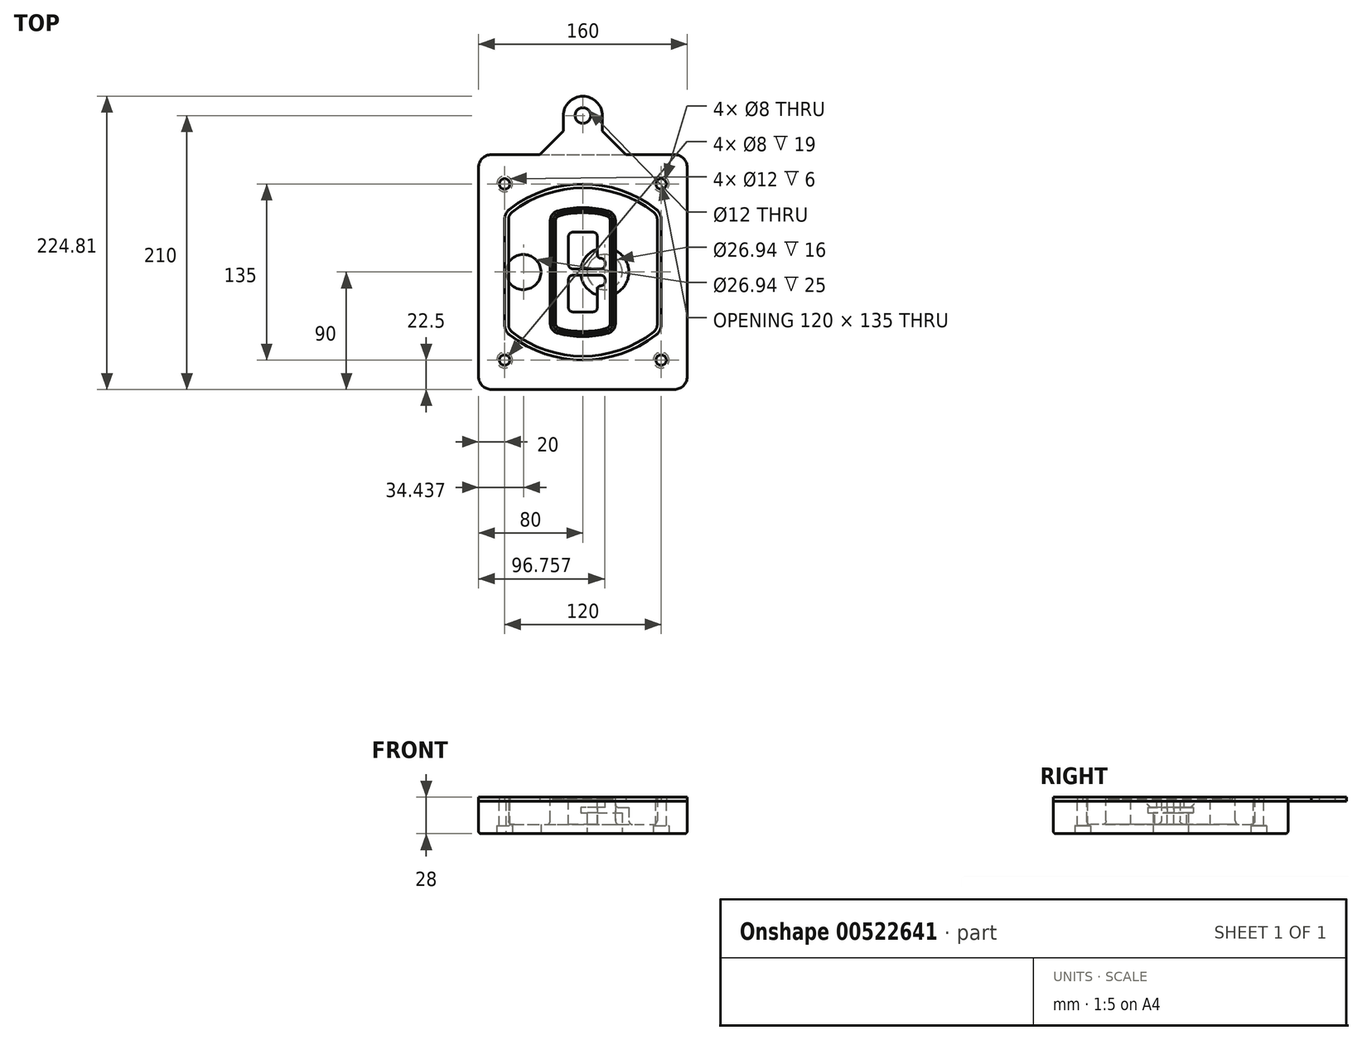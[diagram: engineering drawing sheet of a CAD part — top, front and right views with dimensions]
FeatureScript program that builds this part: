
annotation { "Feature Type Name" : "Feature", "Feature Type Description" : "" }
export const myFeature = defineFeature(function(context is Context, id is Id, definition is map)
    precondition{}
    {
        {
            var Q0;
            Q0=qCreatedBy(makeId("Top.planeOp"),FACE);
            var sketch = newSketch(context, id + "F0", { "sketchPlane" : qUnion([Q0])});
            skPoint(sketch, "E0.rect.middle", {"position": v(0, 0) * mm});
            skLineSegment(sketch, "E1.bottom", {"start": v(-70, -90) * mm, "end": v(70, -90) * mm});
            skLineSegment(sketch, "E1.top", {"start": v(-70, 90) * mm, "end": v(70, 90) * mm});
            skLineSegment(sketch, "E1.left", {"start": v(-80, -80) * mm, "end": v(-80, 80) * mm});
            skLineSegment(sketch, "E1.right", {"start": v(80, -80) * mm, "end": v(80, 80) * mm});
            skLineSegment(sketch, "E2", {"start": v(-80, 90) * mm, "end": v(80, -90) * mm, "construction": true});
            skLineSegment(sketch, "E3", {"start": v(80, 90) * mm, "end": v(-80, -90) * mm, "construction": true});
            skCircle(sketch, "E4", {"center": v(-60, 67.5) * mm, "radius": 4 * mm});
            skCircle(sketch, "E5", {"center": v(60, 67.5) * mm, "radius": 4 * mm});
            skCircle(sketch, "E6", {"center": v(60, -67.5) * mm, "radius": 4 * mm});
            skCircle(sketch, "E7", {"center": v(-60, -67.5) * mm, "radius": 4 * mm});
            skLineSegment(sketch, "E8", {"start": v(-60, 67.5) * mm, "end": v(60, 67.5) * mm, "construction": true});
            skLineSegment(sketch, "E9", {"start": v(60, 67.5) * mm, "end": v(60, -67.5) * mm, "construction": true});
            skLineSegment(sketch, "E10", {"start": v(60, -67.5) * mm, "end": v(-60, -67.5) * mm, "construction": true});
            skLineSegment(sketch, "E11", {"start": v(-60, -67.5) * mm, "end": v(-60, 67.5) * mm, "construction": true});
            skLineSegment(sketch, "E12", {"start": v(-60, 40.3) * mm, "end": v(-60, -40.3) * mm});
            skLineSegment(sketch, "E13", {"start": v(60, 40.3) * mm, "end": v(60, -40.3) * mm});
            skArc(sketch, "E14", {"start": v(56.15, 48.18) * mm, "mid": v(0, 67.5) * mm, "end": v(-56.15, 48.18) * mm});
            skArc(sketch, "E15", {"start": v(-56.15, -48.18) * mm, "mid": v(0, -67.5) * mm, "end": v(56.15, -48.18) * mm});
            skLineSegment(sketch, "E16", {"start": v(-60, 0) * mm, "end": v(60, 0) * mm, "construction": true});
            skPoint(sketch, "E17.visualSharp", {"position": v(-60, -45) * mm});
            skArc(sketch, "E17.filletArc", {"start": v(-60, -40.3) * mm, "mid": v(-58.99, -44.68) * mm, "end": v(-56.15, -48.18) * mm});
            skPoint(sketch, "E18.visualSharp", {"position": v(-60, 45) * mm});
            skArc(sketch, "E18.filletArc", {"start": v(-56.15, 48.18) * mm, "mid": v(-58.99, 44.68) * mm, "end": v(-60, 40.3) * mm});
            skPoint(sketch, "E19.visualSharp", {"position": v(60, 45) * mm});
            skArc(sketch, "E19.filletArc", {"start": v(60, 40.3) * mm, "mid": v(58.99, 44.68) * mm, "end": v(56.15, 48.18) * mm});
            skPoint(sketch, "E20.visualSharp", {"position": v(60, -45) * mm});
            skArc(sketch, "E20.filletArc", {"start": v(56.15, -48.18) * mm, "mid": v(58.99, -44.68) * mm, "end": v(60, -40.3) * mm});
            skPoint(sketch, "E21.visualSharp", {"position": v(-80, 90) * mm});
            skArc(sketch, "E21.filletArc", {"start": v(-70, 90) * mm, "mid": v(-77.07, 87.07) * mm, "end": v(-80, 80) * mm});
            skPoint(sketch, "E22.visualSharp", {"position": v(80, 90) * mm});
            skArc(sketch, "E22.filletArc", {"start": v(80, 80) * mm, "mid": v(77.07, 87.07) * mm, "end": v(70, 90) * mm});
            skPoint(sketch, "E23.visualSharp", {"position": v(80, -90) * mm});
            skArc(sketch, "E23.filletArc", {"start": v(70, -90) * mm, "mid": v(77.07, -87.07) * mm, "end": v(80, -80) * mm});
            skPoint(sketch, "E24.visualSharp", {"position": v(-80, -90) * mm});
            skArc(sketch, "E24.filletArc", {"start": v(-80, -80) * mm, "mid": v(-77.07, -87.07) * mm, "end": v(-70, -90) * mm});
            skArc(sketch, "E25.0", {"start": v(57, 40.3) * mm, "mid": v(56.3, 43.36) * mm, "end": v(54.3, 45.81) * mm});
            skLineSegment(sketch, "E25.1", {"start": v(57, 40.3) * mm, "end": v(57, -40.3) * mm});
            skArc(sketch, "E25.2", {"start": v(54.3, -45.81) * mm, "mid": v(56.3, -43.36) * mm, "end": v(57, -40.3) * mm});
            skArc(sketch, "E25.3", {"start": v(-54.3, -45.81) * mm, "mid": v(0, -64.5) * mm, "end": v(54.3, -45.81) * mm});
            skArc(sketch, "E25.4", {"start": v(-57, -40.3) * mm, "mid": v(-56.3, -43.36) * mm, "end": v(-54.3, -45.81) * mm});
            skArc(sketch, "E25.5", {"start": v(54.3, 45.81) * mm, "mid": v(0, 64.5) * mm, "end": v(-54.3, 45.81) * mm});
            skLineSegment(sketch, "E25.6", {"start": v(-57, 40.3) * mm, "end": v(-57, -40.3) * mm});
            skArc(sketch, "E25.7", {"start": v(-54.3, 45.81) * mm, "mid": v(-56.3, 43.36) * mm, "end": v(-57, 40.3) * mm});
            skArc(sketch, "E26.0", {"start": v(-58.62, 51.33) * mm, "mid": v(-62.58, 46.43) * mm, "end": v(-64, 40.3) * mm});
            skArc(sketch, "E26.1", {"start": v(58.62, 51.33) * mm, "mid": v(0, 71.5) * mm, "end": v(-58.62, 51.33) * mm});
            skArc(sketch, "E26.2", {"start": v(64, 40.3) * mm, "mid": v(62.58, 46.43) * mm, "end": v(58.62, 51.33) * mm});
            skLineSegment(sketch, "E26.3", {"start": v(64, 40.3) * mm, "end": v(64, -40.3) * mm});
            skArc(sketch, "E26.4", {"start": v(58.62, -51.33) * mm, "mid": v(62.58, -46.43) * mm, "end": v(64, -40.3) * mm});
            skLineSegment(sketch, "E26.5", {"start": v(-64, 40.3) * mm, "end": v(-64, -40.3) * mm});
            skArc(sketch, "E26.6", {"start": v(-58.62, -51.33) * mm, "mid": v(0, -71.5) * mm, "end": v(58.62, -51.33) * mm});
            skArc(sketch, "E26.7", {"start": v(-64, -40.3) * mm, "mid": v(-62.58, -46.43) * mm, "end": v(-58.62, -51.33) * mm});
            skSolve(sketch);
        }
        {
            var Q0;
            Q0=makeQuery(id+"F0.imprint","IMPRINT",FACE,{"disambiguationData":[TD([[makeQuery(id+"F0.imprint","IMPRINT",EDGE,{"derivedFrom":sQuery(id+"F0.wireOp",EDGE,"E1.bottom")}),1.0]])]});
            var Q1;
            Q1=makeQuery(id+"F0.imprint","IMPRINT",FACE,{"disambiguationData":[TD([[makeQuery(id+"F0.imprint","IMPRINT",EDGE,{"derivedFrom":sQuery(id+"F0.wireOp",EDGE,"E12")}),1.0]])]});
            var Q2;
            Q2=makeQuery(id+"F0.imprint","IMPRINT",FACE,{"disambiguationData":[TD([[makeQuery(id+"F0.imprint","IMPRINT",EDGE,{"derivedFrom":sQuery(id+"F0.wireOp",EDGE,"E25.0")}),1.0]])]});
            var Q3;
            Q3=makeQuery(id+"F0.imprint","IMPRINT",FACE,{"disambiguationData":[TD([[makeQuery(id+"F0.imprint","IMPRINT",EDGE,{"derivedFrom":sQuery(id+"F0.wireOp",EDGE,"E12")}),-1.0]])]});
            extrude(context, id + "F1", {"entities" : qUnion([Q0, Q1, Q2, Q3]), "oppositeDirection" : true, "depth" : 25 * mm});
        }
        {
            var Q0;
            Q0=makeQuery(id+"F0.imprint","IMPRINT",FACE,{"disambiguationData":[TD([[makeQuery(id+"F0.imprint","IMPRINT",EDGE,{"derivedFrom":sQuery(id+"F0.wireOp",EDGE,"E12")}),1.0]])]});
            extrude(context, id + "F2", {"entities" : qUnion([Q0]), "operationType" : NewBodyOperationType.ADD, "depth" : 3 * mm});
        }
        {
            var Q0;
            Q0=makeQuery(id+"F0.imprint","IMPRINT",FACE,{"disambiguationData":[TD([[makeQuery(id+"F0.imprint","IMPRINT",EDGE,{"derivedFrom":sQuery(id+"F0.wireOp",EDGE,"E25.0")}),1.0]])]});
            extrude(context, id + "F3", {"entities" : qUnion([Q0]), "operationType" : NewBodyOperationType.REMOVE, "oppositeDirection" : true, "depth" : 18 * mm});
        }
        {
            var Q0;
            Q0=makeQuery(id+"F2.opExtrude","CAP_FACE",FACE,{"disambiguationData":[OSD([sQuery(id+"F0.wireOp",EDGE,"E12"),sQuery(id+"F0.wireOp",EDGE,"E13"),sQuery(id+"F0.wireOp",EDGE,"E14"),sQuery(id+"F0.wireOp",EDGE,"E15"),sQuery(id+"F0.wireOp",EDGE,"E17.filletArc"),sQuery(id+"F0.wireOp",EDGE,"E18.filletArc"),sQuery(id+"F0.wireOp",EDGE,"E19.filletArc"),sQuery(id+"F0.wireOp",EDGE,"E20.filletArc"),sQuery(id+"F0.wireOp",EDGE,"E25.0"),sQuery(id+"F0.wireOp",EDGE,"E25.1"),sQuery(id+"F0.wireOp",EDGE,"E25.2"),sQuery(id+"F0.wireOp",EDGE,"E25.3"),sQuery(id+"F0.wireOp",EDGE,"E25.4"),sQuery(id+"F0.wireOp",EDGE,"E25.5"),sQuery(id+"F0.wireOp",EDGE,"E25.6"),sQuery(id+"F0.wireOp",EDGE,"E25.7")])],"isStart":false});
            var sketch = newSketch(context, id + "F4", { "sketchPlane" : qUnion([Q0])});
            skArc(sketch, "E27.0", {"start": v(-19.08, -46.97) * mm, "mid": v(0, -49.5) * mm, "end": v(19.08, -46.97) * mm});
            skArc(sketch, "E28.0", {"start": v(19.08, 46.97) * mm, "mid": v(0, 49.5) * mm, "end": v(-19.08, 46.97) * mm});
            skLineSegment(sketch, "E29", {"start": v(-25, 39.25) * mm, "end": v(-25, -39.25) * mm});
            skLineSegment(sketch, "E30", {"start": v(25, 39.25) * mm, "end": v(25, -39.25) * mm});
            skLineSegment(sketch, "E31", {"start": v(-25, 45.1) * mm, "end": v(25, 45.1) * mm, "construction": true});
            skLineSegment(sketch, "E32", {"start": v(-25, -45.1) * mm, "end": v(25, -45.1) * mm, "construction": true});
            skPoint(sketch, "E33.visualSharp", {"position": v(-25, 45.1) * mm});
            skArc(sketch, "E33.filletArc", {"start": v(-19.08, 46.97) * mm, "mid": v(-23.35, 44.11) * mm, "end": v(-25, 39.25) * mm});
            skPoint(sketch, "E34.visualSharp", {"position": v(25, 45.1) * mm});
            skArc(sketch, "E34.filletArc", {"start": v(25, 39.25) * mm, "mid": v(23.35, 44.11) * mm, "end": v(19.08, 46.97) * mm});
            skPoint(sketch, "E35.visualSharp", {"position": v(25, -45.1) * mm});
            skArc(sketch, "E35.filletArc", {"start": v(19.08, -46.97) * mm, "mid": v(23.35, -44.11) * mm, "end": v(25, -39.25) * mm});
            skPoint(sketch, "E36.visualSharp", {"position": v(-25, -45.1) * mm});
            skArc(sketch, "E36.filletArc", {"start": v(-25, -39.25) * mm, "mid": v(-23.35, -44.11) * mm, "end": v(-19.08, -46.97) * mm});
            skArc(sketch, "E37.0", {"start": v(54.3, 45.81) * mm, "mid": v(0, 64.5) * mm, "end": v(-54.3, 45.81) * mm});
            skArc(sketch, "E37.1", {"start": v(-54.3, 45.81) * mm, "mid": v(-56.3, 43.36) * mm, "end": v(-57, 40.3) * mm});
            skLineSegment(sketch, "E37.2", {"start": v(-57, 40.3) * mm, "end": v(-57, -40.3) * mm});
            skArc(sketch, "E37.3", {"start": v(-57, -40.3) * mm, "mid": v(-56.3, -43.36) * mm, "end": v(-54.3, -45.81) * mm});
            skArc(sketch, "E37.4", {"start": v(-54.3, -45.81) * mm, "mid": v(0, -64.5) * mm, "end": v(54.3, -45.81) * mm});
            skArc(sketch, "E37.5", {"start": v(54.3, -45.81) * mm, "mid": v(56.3, -43.36) * mm, "end": v(57, -40.3) * mm});
            skLineSegment(sketch, "E37.6", {"start": v(57, 40.3) * mm, "end": v(57, -40.3) * mm});
            skArc(sketch, "E37.7", {"start": v(57, 40.3) * mm, "mid": v(56.3, 43.36) * mm, "end": v(54.3, 45.81) * mm});
            skLineSegment(sketch, "E38.0", {"start": v(23, 39.25) * mm, "end": v(23, -39.25) * mm});
            skArc(sketch, "E38.1", {"start": v(18.56, -45.04) * mm, "mid": v(21.76, -42.9) * mm, "end": v(23, -39.25) * mm});
            skArc(sketch, "E38.2", {"start": v(-18.56, -45.04) * mm, "mid": v(0, -47.5) * mm, "end": v(18.56, -45.04) * mm});
            skArc(sketch, "E38.3", {"start": v(-23, -39.25) * mm, "mid": v(-21.76, -42.9) * mm, "end": v(-18.56, -45.04) * mm});
            skLineSegment(sketch, "E38.4", {"start": v(-23, 39.25) * mm, "end": v(-23, -39.25) * mm});
            skArc(sketch, "E38.5", {"start": v(23, 39.25) * mm, "mid": v(21.76, 42.9) * mm, "end": v(18.56, 45.04) * mm});
            skArc(sketch, "E38.6", {"start": v(-18.56, 45.04) * mm, "mid": v(-21.76, 42.9) * mm, "end": v(-23, 39.25) * mm});
            skArc(sketch, "E38.7", {"start": v(18.56, 45.04) * mm, "mid": v(0, 47.5) * mm, "end": v(-18.56, 45.04) * mm});
            skArc(sketch, "E39.0", {"start": v(21, 39.25) * mm, "mid": v(20.18, 41.68) * mm, "end": v(18.04, 43.1) * mm});
            skLineSegment(sketch, "E39.1", {"start": v(21, 39.25) * mm, "end": v(21, -39.25) * mm});
            skArc(sketch, "E39.2", {"start": v(18.04, -43.1) * mm, "mid": v(20.18, -41.68) * mm, "end": v(21, -39.25) * mm});
            skArc(sketch, "E39.3", {"start": v(-18.04, -43.1) * mm, "mid": v(0, -45.5) * mm, "end": v(18.04, -43.1) * mm});
            skArc(sketch, "E39.4", {"start": v(-21, -39.25) * mm, "mid": v(-20.18, -41.68) * mm, "end": v(-18.04, -43.1) * mm});
            skArc(sketch, "E39.5", {"start": v(18.04, 43.1) * mm, "mid": v(0, 45.5) * mm, "end": v(-18.04, 43.1) * mm});
            skLineSegment(sketch, "E39.6", {"start": v(-21, 39.25) * mm, "end": v(-21, -39.25) * mm});
            skArc(sketch, "E39.7", {"start": v(-18.04, 43.1) * mm, "mid": v(-20.18, 41.68) * mm, "end": v(-21, 39.25) * mm});
            skLineSegment(sketch, "E40", {"start": v(-25, 0) * mm, "end": v(25, 0) * mm, "construction": true});
            skLineSegment(sketch, "E41", {"start": v(-11, 5.5) * mm, "end": v(-11, 27.5) * mm});
            skLineSegment(sketch, "E42", {"start": v(-8, 30.5) * mm, "end": v(8, 30.5) * mm});
            skLineSegment(sketch, "E43", {"start": v(11, 27.5) * mm, "end": v(11, 13.5) * mm});
            skLineSegment(sketch, "E44", {"start": v(14, 10.5) * mm, "end": v(14, 10.5) * mm});
            skLineSegment(sketch, "E45", {"start": v(17, 7.5) * mm, "end": v(17, 5.5) * mm});
            skLineSegment(sketch, "E46", {"start": v(14, 2.5) * mm, "end": v(-8, 2.5) * mm});
            skPoint(sketch, "E47.visualSharp", {"position": v(-11, 30.5) * mm});
            skArc(sketch, "E47.filletArc", {"start": v(-8, 30.5) * mm, "mid": v(-10.12, 29.62) * mm, "end": v(-11, 27.5) * mm});
            skPoint(sketch, "E48.visualSharp", {"position": v(11, 30.5) * mm});
            skArc(sketch, "E48.filletArc", {"start": v(11, 27.5) * mm, "mid": v(10.12, 29.62) * mm, "end": v(8, 30.5) * mm});
            skPoint(sketch, "E49.visualSharp", {"position": v(11, 10.5) * mm});
            skArc(sketch, "E49.filletArc", {"start": v(11, 13.5) * mm, "mid": v(11.88, 11.38) * mm, "end": v(14, 10.5) * mm});
            skPoint(sketch, "E50.visualSharp", {"position": v(17, 10.5) * mm});
            skArc(sketch, "E50.filletArc", {"start": v(17, 7.5) * mm, "mid": v(16.12, 9.62) * mm, "end": v(14, 10.5) * mm});
            skPoint(sketch, "E51.visualSharp", {"position": v(17, 2.5) * mm});
            skArc(sketch, "E51.filletArc", {"start": v(14, 2.5) * mm, "mid": v(16.12, 3.38) * mm, "end": v(17, 5.5) * mm});
            skPoint(sketch, "E52.visualSharp", {"position": v(-11, 2.5) * mm});
            skArc(sketch, "E52.filletArc", {"start": v(-11, 5.5) * mm, "mid": v(-10.12, 3.38) * mm, "end": v(-8, 2.5) * mm});
            skLineSegment(sketch, "E53.0.MirrorCS", {"start": v(14, -2.5) * mm, "end": v(-8, -2.5) * mm});
            skArc(sketch, "E54.0.MirrorCS", {"start": v(-11, -5.5) * mm, "mid": v(-10.12, -3.38) * mm, "end": v(-8, -2.5) * mm});
            skLineSegment(sketch, "E55.0.MirrorCS", {"start": v(-11, -5.5) * mm, "end": v(-11, -27.5) * mm});
            skArc(sketch, "E56.0.MirrorCS", {"start": v(-8, -30.5) * mm, "mid": v(-10.12, -29.62) * mm, "end": v(-11, -27.5) * mm});
            skLineSegment(sketch, "E57.0.MirrorCS", {"start": v(-8, -30.5) * mm, "end": v(8, -30.5) * mm});
            skArc(sketch, "E58.0.MirrorCS", {"start": v(11, -27.5) * mm, "mid": v(10.12, -29.62) * mm, "end": v(8, -30.5) * mm});
            skLineSegment(sketch, "E59.0.MirrorCS", {"start": v(11, -27.5) * mm, "end": v(11, -13.5) * mm});
            skArc(sketch, "E60.0.MirrorCS", {"start": v(11, -13.5) * mm, "mid": v(11.88, -11.38) * mm, "end": v(14, -10.5) * mm});
            skArc(sketch, "E61.0.MirrorCS", {"start": v(17, -7.5) * mm, "mid": v(16.12, -9.62) * mm, "end": v(14, -10.5) * mm});
            skLineSegment(sketch, "E62.0.MirrorCS", {"start": v(17, -7.5) * mm, "end": v(17, -5.5) * mm});
            skArc(sketch, "E63.0.MirrorCS", {"start": v(14, -2.5) * mm, "mid": v(16.12, -3.38) * mm, "end": v(17, -5.5) * mm});
            skSolve(sketch);
        }
        {
            var Q0;
            Q0=makeQuery(id+"F4.imprint","IMPRINT",FACE,{"disambiguationData":[TD([[makeQuery(id+"F4.imprint","IMPRINT",EDGE,{"derivedFrom":sQuery(id+"F4.wireOp",EDGE,"E27.0")}),1.0]])]});
            var Q1;
            Q1=makeQuery(id+"F4.imprint","IMPRINT",FACE,{"disambiguationData":[TD([[makeQuery(id+"F4.imprint","IMPRINT",EDGE,{"derivedFrom":sQuery(id+"F4.wireOp",EDGE,"E38.0")}),-1.0]])]});
            var Q2;
            Q2=makeQuery(id+"F4.imprint","IMPRINT",FACE,{"disambiguationData":[TD([[makeQuery(id+"F4.imprint","IMPRINT",EDGE,{"derivedFrom":sQuery(id+"F4.wireOp",EDGE,"E39.0")}),1.0]])]});
            extrude(context, id + "F5", {"entities" : qUnion([Q0, Q1, Q2]), "operationType" : NewBodyOperationType.ADD, "endBound" : BoundingType.UP_TO_NEXT, "oppositeDirection" : true, "depth" : 25 * mm});
        }
        {
            var Q0;
            Q0=makeQuery(id+"F4.imprint","IMPRINT",FACE,{"disambiguationData":[TD([[makeQuery(id+"F4.imprint","IMPRINT",EDGE,{"derivedFrom":sQuery(id+"F4.wireOp",EDGE,"E38.0")}),-1.0]])]});
            extrude(context, id + "F6", {"entities" : qUnion([Q0]), "operationType" : NewBodyOperationType.REMOVE, "oppositeDirection" : true, "depth" : 2 * mm});
        }
        {
            var Q0;
            Q0=makeQuery(id+"F1.opExtrude","CAP_FACE",FACE,{"disambiguationData":[OSD([sQuery(id+"F0.wireOp",EDGE,"E1.bottom"),sQuery(id+"F0.wireOp",EDGE,"E1.top"),sQuery(id+"F0.wireOp",EDGE,"E1.left"),sQuery(id+"F0.wireOp",EDGE,"E1.right"),sQuery(id+"F0.wireOp",EDGE,"E4"),sQuery(id+"F0.wireOp",EDGE,"E5"),sQuery(id+"F0.wireOp",EDGE,"E6"),sQuery(id+"F0.wireOp",EDGE,"E7"),sQuery(id+"F0.wireOp",EDGE,"E21.filletArc"),sQuery(id+"F0.wireOp",EDGE,"E22.filletArc"),sQuery(id+"F0.wireOp",EDGE,"E23.filletArc"),sQuery(id+"F0.wireOp",EDGE,"E24.filletArc")])],"isStart":false});
            var sketch = newSketch(context, id + "F7", { "sketchPlane" : qUnion([Q0])});
            skCircle(sketch, "E64", {"center": v(16.76, 0) * mm, "radius": 13.47 * mm});
            skCircle(sketch, "E65", {"center": v(-45.56, 0) * mm, "radius": 13.47 * mm});
            skLineSegment(sketch, "E66", {"start": v(80, 0) * mm, "end": v(-80, 0) * mm});
            skCircle(sketch, "E67", {"center": v(16.76, 0) * mm, "radius": 18.47 * mm});
            skCircle(sketch, "E68", {"center": v(60, -67.5) * mm, "radius": 6 * mm});
            skCircle(sketch, "E69", {"center": v(-60, -67.5) * mm, "radius": 6 * mm});
            skCircle(sketch, "E70", {"center": v(-60, 67.5) * mm, "radius": 6 * mm});
            skCircle(sketch, "E71", {"center": v(60, 67.5) * mm, "radius": 6 * mm});
            skSolve(sketch);
        }
        {
            var Q0;
            {var subQ1=sQuery(id+"F7.wireOp",EDGE,"E66");var subQ4=sQuery(id+"F7.wireOp",EDGE,"E64");var subQ6=makeQuery(id+"F7.imprint","INTERSECT",VERTEX,{"disambiguationData":[OD(0.0)],"derivedFrom":[subQ4,subQ1]});Q0=makeQuery(id+"F7.imprint","IMPRINT",FACE,{"disambiguationData":[TD([[makeQuery(id+"F7.imprint","IMPRINT",EDGE,{"disambiguationData":[TD([[subQ6,-1.0]])],"derivedFrom":subQ4}),-1.0]])]});}
            var Q1;
            {var subQ0=sQuery(id+"F7.wireOp",EDGE,"E66");var subQ1=sQuery(id+"F7.wireOp",EDGE,"E64");var subQ3=makeQuery(id+"F7.imprint","INTERSECT",VERTEX,{"disambiguationData":[OD(0.0)],"derivedFrom":[subQ1,subQ0]});Q1=makeQuery(id+"F7.imprint","IMPRINT",FACE,{"disambiguationData":[TD([[makeQuery(id+"F7.imprint","IMPRINT",EDGE,{"disambiguationData":[TD([[subQ3,-1.0]])],"derivedFrom":subQ1}),1.0]])]});}
            var Q2;
            {var subQ0=sQuery(id+"F7.wireOp",EDGE,"E66");var subQ1=sQuery(id+"F7.wireOp",EDGE,"E64");var subQ3=makeQuery(id+"F7.imprint","INTERSECT",VERTEX,{"disambiguationData":[OD(0.0)],"derivedFrom":[subQ1,subQ0]});Q2=makeQuery(id+"F7.imprint","IMPRINT",FACE,{"disambiguationData":[TD([[makeQuery(id+"F7.imprint","IMPRINT",EDGE,{"disambiguationData":[TD([[subQ3,1.0]])],"derivedFrom":subQ1}),1.0]])]});}
            var Q3;
            {var subQ1=sQuery(id+"F7.wireOp",EDGE,"E66");var subQ4=sQuery(id+"F7.wireOp",EDGE,"E64");var subQ6=makeQuery(id+"F7.imprint","INTERSECT",VERTEX,{"disambiguationData":[OD(0.0)],"derivedFrom":[subQ4,subQ1]});Q3=makeQuery(id+"F7.imprint","IMPRINT",FACE,{"disambiguationData":[TD([[makeQuery(id+"F7.imprint","IMPRINT",EDGE,{"disambiguationData":[TD([[subQ6,1.0]])],"derivedFrom":subQ4}),-1.0]])]});}
            extrude(context, id + "F8", {"entities" : qUnion([Q0, Q1, Q2, Q3]), "operationType" : NewBodyOperationType.ADD, "oppositeDirection" : true, "depth" : 20 * mm});
        }
        {
            var Q0;
            {var subQ0=sQuery(id+"F7.wireOp",EDGE,"E66");var subQ1=sQuery(id+"F7.wireOp",EDGE,"E64");var subQ3=makeQuery(id+"F7.imprint","INTERSECT",VERTEX,{"disambiguationData":[OD(0.0)],"derivedFrom":[subQ1,subQ0]});Q0=makeQuery(id+"F7.imprint","IMPRINT",FACE,{"disambiguationData":[TD([[makeQuery(id+"F7.imprint","IMPRINT",EDGE,{"disambiguationData":[TD([[subQ3,-1.0]])],"derivedFrom":subQ1}),1.0]])]});}
            var Q1;
            {var subQ0=sQuery(id+"F7.wireOp",EDGE,"E66");var subQ1=sQuery(id+"F7.wireOp",EDGE,"E64");var subQ3=makeQuery(id+"F7.imprint","INTERSECT",VERTEX,{"disambiguationData":[OD(0.0)],"derivedFrom":[subQ1,subQ0]});Q1=makeQuery(id+"F7.imprint","IMPRINT",FACE,{"disambiguationData":[TD([[makeQuery(id+"F7.imprint","IMPRINT",EDGE,{"disambiguationData":[TD([[subQ3,1.0]])],"derivedFrom":subQ1}),1.0]])]});}
            extrude(context, id + "F9", {"entities" : qUnion([Q0, Q1]), "operationType" : NewBodyOperationType.REMOVE, "oppositeDirection" : true, "depth" : 16 * mm});
        }
        {
            var Q0;
            {var subQ0=sQuery(id+"F7.wireOp",EDGE,"E66");var subQ1=sQuery(id+"F7.wireOp",EDGE,"E65");var subQ3=makeQuery(id+"F7.imprint","INTERSECT",VERTEX,{"disambiguationData":[OD(0.0)],"derivedFrom":[subQ1,subQ0]});Q0=makeQuery(id+"F7.imprint","IMPRINT",FACE,{"disambiguationData":[TD([[makeQuery(id+"F7.imprint","IMPRINT",EDGE,{"disambiguationData":[TD([[subQ3,-1.0]])],"derivedFrom":subQ1}),1.0]])]});}
            var Q1;
            {var subQ0=sQuery(id+"F7.wireOp",EDGE,"E66");var subQ1=sQuery(id+"F7.wireOp",EDGE,"E65");var subQ3=makeQuery(id+"F7.imprint","INTERSECT",VERTEX,{"disambiguationData":[OD(0.0)],"derivedFrom":[subQ1,subQ0]});Q1=makeQuery(id+"F7.imprint","IMPRINT",FACE,{"disambiguationData":[TD([[makeQuery(id+"F7.imprint","IMPRINT",EDGE,{"disambiguationData":[TD([[subQ3,1.0]])],"derivedFrom":subQ1}),1.0]])]});}
            extrude(context, id + "F10", {"entities" : qUnion([Q0, Q1]), "operationType" : NewBodyOperationType.REMOVE, "oppositeDirection" : true, "depth" : 25 * mm});
        }
        {
            var Q0;
            Q0=makeQuery(id+"F7.imprint","IMPRINT",FACE,{"disambiguationData":[TD([[makeQuery(id+"F7.imprint","IMPRINT",EDGE,{"derivedFrom":sQuery(id+"F7.wireOp",EDGE,"E68")}),1.0]])]});
            var Q1;
            Q1=makeQuery(id+"F7.imprint","IMPRINT",FACE,{"disambiguationData":[TD([[makeQuery(id+"F7.imprint","IMPRINT",EDGE,{"derivedFrom":makeQuery(id+"F1.opExtrude","CAP_EDGE",EDGE,{"disambiguationData":[OSD([sQuery(id+"F0.wireOp",EDGE,"E5")])],"isStart":false})}),-1.0]])]});
            var Q2;
            Q2=makeQuery(id+"F7.imprint","IMPRINT",FACE,{"disambiguationData":[TD([[makeQuery(id+"F7.imprint","IMPRINT",EDGE,{"derivedFrom":sQuery(id+"F7.wireOp",EDGE,"E69")}),1.0]])]});
            var Q3;
            Q3=makeQuery(id+"F7.imprint","IMPRINT",FACE,{"disambiguationData":[TD([[makeQuery(id+"F7.imprint","IMPRINT",EDGE,{"derivedFrom":makeQuery(id+"F1.opExtrude","CAP_EDGE",EDGE,{"disambiguationData":[OSD([sQuery(id+"F0.wireOp",EDGE,"E4")])],"isStart":false})}),-1.0]])]});
            var Q4;
            Q4=makeQuery(id+"F7.imprint","IMPRINT",FACE,{"disambiguationData":[TD([[makeQuery(id+"F7.imprint","IMPRINT",EDGE,{"derivedFrom":sQuery(id+"F7.wireOp",EDGE,"E70")}),1.0]])]});
            var Q5;
            Q5=makeQuery(id+"F7.imprint","IMPRINT",FACE,{"disambiguationData":[TD([[makeQuery(id+"F7.imprint","IMPRINT",EDGE,{"derivedFrom":makeQuery(id+"F1.opExtrude","CAP_EDGE",EDGE,{"disambiguationData":[OSD([sQuery(id+"F0.wireOp",EDGE,"E7")])],"isStart":false})}),-1.0]])]});
            var Q6;
            Q6=makeQuery(id+"F7.imprint","IMPRINT",FACE,{"disambiguationData":[TD([[makeQuery(id+"F7.imprint","IMPRINT",EDGE,{"derivedFrom":sQuery(id+"F7.wireOp",EDGE,"E71")}),1.0]])]});
            var Q7;
            Q7=makeQuery(id+"F7.imprint","IMPRINT",FACE,{"disambiguationData":[TD([[makeQuery(id+"F7.imprint","IMPRINT",EDGE,{"derivedFrom":makeQuery(id+"F1.opExtrude","CAP_EDGE",EDGE,{"disambiguationData":[OSD([sQuery(id+"F0.wireOp",EDGE,"E6")])],"isStart":false})}),-1.0]])]});
            extrude(context, id + "F11", {"entities" : qUnion([Q0, Q1, Q2, Q3, Q4, Q5, Q6, Q7]), "operationType" : NewBodyOperationType.REMOVE, "oppositeDirection" : true, "depth" : 6 * mm});
        }
        {
            var Q0;
            Q0=makeQuery(id+"F9.boolean.opBoolean","COPY",FACE,{"derivedFrom":makeQuery(id+"F9.opExtrude","CAP_FACE",FACE,{"disambiguationData":[OSD([sQuery(id+"F7.wireOp",EDGE,"E64")])],"isStart":false})});
            var sketch = newSketch(context, id + "F12", { "sketchPlane" : qUnion([Q0])});
            skArc(sketch, "E72.0", {"start": v(11, 17.55) * mm, "mid": v(2.57, 11.82) * mm, "end": v(-1.54, 2.5) * mm});
            skArc(sketch, "E72.1", {"start": v(-1.54, -2.5) * mm, "mid": v(2.57, -11.82) * mm, "end": v(11, -17.55) * mm});
            skLineSegment(sketch, "E73", {"start": v(-1.54, -2.5) * mm, "end": v(14, -2.5) * mm});
            skLineSegment(sketch, "E74.0", {"start": v(14, 2.5) * mm, "end": v(-1.54, 2.5) * mm});
            skArc(sketch, "E74.1", {"start": v(14, 2.5) * mm, "mid": v(16.12, 3.38) * mm, "end": v(17, 5.5) * mm});
            skLineSegment(sketch, "E74.2", {"start": v(17, 7.5) * mm, "end": v(17, 5.5) * mm});
            skArc(sketch, "E74.3", {"start": v(17, 7.5) * mm, "mid": v(16.12, 9.62) * mm, "end": v(14, 10.5) * mm});
            skArc(sketch, "E74.4", {"start": v(11, 13.5) * mm, "mid": v(11.88, 11.38) * mm, "end": v(14, 10.5) * mm});
            skLineSegment(sketch, "E74.5", {"start": v(11, 17.55) * mm, "end": v(11, 13.5) * mm});
            skLineSegment(sketch, "E74.7", {"start": v(14, -2.5) * mm, "end": v(-1.54, -2.5) * mm});
            skArc(sketch, "E74.8", {"start": v(14, -2.5) * mm, "mid": v(16.12, -3.38) * mm, "end": v(17, -5.5) * mm});
            skLineSegment(sketch, "E74.9", {"start": v(17, -7.5) * mm, "end": v(17, -5.5) * mm});
            skArc(sketch, "E74.10", {"start": v(17, -7.5) * mm, "mid": v(16.12, -9.62) * mm, "end": v(14, -10.5) * mm});
            skArc(sketch, "E74.11", {"start": v(11, -13.5) * mm, "mid": v(11.88, -11.38) * mm, "end": v(14, -10.5) * mm});
            skLineSegment(sketch, "E74.12", {"start": v(11, -17.55) * mm, "end": v(11, -13.5) * mm});
            skPoint(sketch, "E75.orphan", {"position": v(11, -27.5) * mm});
            skPoint(sketch, "E76.orphan", {"position": v(-8, -2.5) * mm});
            skPoint(sketch, "E77.orphan", {"position": v(-8, 2.5) * mm});
            skPoint(sketch, "E78.orphan", {"position": v(11, 27.5) * mm});
            skSolve(sketch);
        }
        {
            var Q0;
            {var subQ7=sQuery(id+"F12.wireOp",EDGE,"E72.0");var subQ14=sQuery(id+"F12.wireOp",EDGE,"E72.1");var subQ16=sQuery(id+"F12.wireOp",EDGE,"E74.1");var subQ18=sQuery(id+"F12.wireOp",EDGE,"E74.8");Q0=qUnion([makeQuery(id+"F12.imprint","IMPRINT",FACE,{"disambiguationData":[TD([[makeQuery(id+"F12.imprint","IMPRINT",EDGE,{"derivedFrom":subQ7}),1.0]])]}),makeQuery(id+"F12.imprint","IMPRINT",FACE,{"disambiguationData":[TD([[makeQuery(id+"F12.imprint","IMPRINT",EDGE,{"derivedFrom":subQ14}),1.0]])]}),makeQuery(id+"F12.imprint","IMPRINT",FACE,{"disambiguationData":[TD([[makeQuery(id+"F12.imprint","IMPRINT",EDGE,{"derivedFrom":subQ16}),1.0]])]}),makeQuery(id+"F12.imprint","IMPRINT",FACE,{"disambiguationData":[TD([[makeQuery(id+"F12.imprint","IMPRINT",EDGE,{"derivedFrom":subQ18}),-1.0]])]})]);}
            var Q1;
            Q1=makeQuery(id+"F5.boolean.opBoolean","SPLIT",FACE,{"disambiguationData":[TD([makeQuery(id+"F5.opExtrude","SWEPT_FACE",FACE,{"disambiguationData":[OSD([sQuery(id+"F4.wireOp",EDGE,"E41")])]})])],"derivedFrom":makeQuery(id+"F3.boolean.opBoolean","COPY",FACE,{"derivedFrom":makeQuery(id+"F3.opExtrude","CAP_FACE",FACE,{"disambiguationData":[OSD([sQuery(id+"F0.wireOp",EDGE,"E25.0"),sQuery(id+"F0.wireOp",EDGE,"E25.1"),sQuery(id+"F0.wireOp",EDGE,"E25.2"),sQuery(id+"F0.wireOp",EDGE,"E25.3"),sQuery(id+"F0.wireOp",EDGE,"E25.4"),sQuery(id+"F0.wireOp",EDGE,"E25.5"),sQuery(id+"F0.wireOp",EDGE,"E25.6"),sQuery(id+"F0.wireOp",EDGE,"E25.7")])],"isStart":false})})});
            extrude(context, id + "F13", {"entities" : qUnion([Q0]), "operationType" : NewBodyOperationType.REMOVE, "endBound" : BoundingType.UP_TO_SURFACE, "endBoundEntityFace" : qUnion([Q1]), "depth" : 25 * mm});
        }
        {
            var Q0;
            Q0=makeQuery(id+"F3.boolean.opBoolean","COPY",EDGE,{"derivedFrom":makeQuery(id+"F3.opExtrude","CAP_EDGE",EDGE,{"disambiguationData":[OSD([sQuery(id+"F0.wireOp",EDGE,"E25.6")])],"isStart":false})});
            var Q1;
            Q1=makeQuery(id+"F8.boolean.opBoolean","INTERSECT",EDGE,{"derivedFrom":[makeQuery(id+"F5.opExtrude","SWEPT_FACE",FACE,{"disambiguationData":[OSD([sQuery(id+"F4.wireOp",EDGE,"E30")])]}),makeQuery(id+"F8.opExtrude","CAP_FACE",FACE,{"disambiguationData":[OSD([sQuery(id+"F7.wireOp",EDGE,"E67")])],"isStart":false})]});
            var Q2;
            Q2=makeQuery(id+"F8.boolean.opBoolean","INTERSECT",EDGE,{"disambiguationData":[OD(1.0)],"derivedFrom":[makeQuery(id+"F5.opExtrude","SWEPT_FACE",FACE,{"disambiguationData":[OSD([sQuery(id+"F4.wireOp",EDGE,"E30")])]}),makeQuery(id+"F8.opExtrude","SWEPT_FACE",FACE,{"disambiguationData":[OSD([sQuery(id+"F7.wireOp",EDGE,"E67")])]})]});
            var Q3;
            {var subQ0=sQuery(id+"F4.wireOp",EDGE,"E30");Q3=makeQuery(id+"F8.boolean.opBoolean","SPLIT",EDGE,{"disambiguationData":[TD([makeQuery(id+"F5.opExtrude","SWEPT_FACE",FACE,{"disambiguationData":[OSD([sQuery(id+"F4.wireOp",EDGE,"E35.filletArc")])]})])],"derivedFrom":makeQuery(id+"F5.opExtrude","CAP_EDGE",EDGE,{"disambiguationData":[OSD([subQ0])],"isStart":false})});}
            var Q4;
            {var subQ0=sQuery(id+"F0.wireOp",EDGE,"E25.7");var subQ1=sQuery(id+"F0.wireOp",EDGE,"E25.1");var subQ2=sQuery(id+"F0.wireOp",EDGE,"E25.6");var subQ3=sQuery(id+"F0.wireOp",EDGE,"E25.5");var subQ4=sQuery(id+"F0.wireOp",EDGE,"E25.4");var subQ5=sQuery(id+"F0.wireOp",EDGE,"E25.0");var subQ6=sQuery(id+"F0.wireOp",EDGE,"E25.2");var subQ7=sQuery(id+"F0.wireOp",EDGE,"E25.3");Q4=makeQuery(id+"F8.boolean.opBoolean","INTERSECT",EDGE,{"derivedFrom":[makeQuery(id+"F5.boolean.opBoolean","SPLIT",FACE,{"disambiguationData":[TD([makeQuery(id+"F2.opExtrude","SWEPT_FACE",FACE,{"disambiguationData":[OSD([subQ5])]})])],"derivedFrom":makeQuery(id+"F3.boolean.opBoolean","COPY",FACE,{"derivedFrom":makeQuery(id+"F3.opExtrude","CAP_FACE",FACE,{"disambiguationData":[OSD([subQ5,subQ1,subQ6,subQ7,subQ4,subQ3,subQ2,subQ0])],"isStart":false})})}),makeQuery(id+"F8.opExtrude","SWEPT_FACE",FACE,{"disambiguationData":[OSD([sQuery(id+"F7.wireOp",EDGE,"E67")])]})]});}
            var Q5;
            Q5=makeQuery(id+"F8.boolean.opBoolean","INTERSECT",EDGE,{"disambiguationData":[OD(0.0)],"derivedFrom":[makeQuery(id+"F5.opExtrude","SWEPT_FACE",FACE,{"disambiguationData":[OSD([sQuery(id+"F4.wireOp",EDGE,"E30")])]}),makeQuery(id+"F8.opExtrude","SWEPT_FACE",FACE,{"disambiguationData":[OSD([sQuery(id+"F7.wireOp",EDGE,"E67")])]})]});
            fillet(context, id + "F14", {"entities" : qUnion([Q0, Q1, Q2, Q3, Q4, Q5]), "radius" : 3 * mm, "tangentPropagation" : true, "allowEdgeOverflow" : false});
        }
        {
            var Q0;
            Q0=makeQuery(id+"F1.opExtrude","CAP_EDGE",EDGE,{"disambiguationData":[OSD([sQuery(id+"F0.wireOp",EDGE,"E1.bottom")])],"isStart":false});
            fillet(context, id + "F15", {"entities" : qUnion([Q0]), "radius" : 2 * mm, "tangentPropagation" : true, "allowEdgeOverflow" : false});
        }
        {
            var Q0;
            {var subQ0=sQuery(id+"F0.wireOp",EDGE,"E21.filletArc");var subQ1=sQuery(id+"F0.wireOp",EDGE,"E7");var subQ2=sQuery(id+"F0.wireOp",EDGE,"E6");var subQ3=sQuery(id+"F0.wireOp",EDGE,"E5");var subQ4=sQuery(id+"F0.wireOp",EDGE,"E4");var subQ5=sQuery(id+"F0.wireOp",EDGE,"E22.filletArc");var subQ6=sQuery(id+"F0.wireOp",EDGE,"E1.bottom");var subQ7=sQuery(id+"F0.wireOp",EDGE,"E1.right");var subQ8=sQuery(id+"F0.wireOp",EDGE,"E1.top");var subQ9=sQuery(id+"F0.wireOp",EDGE,"E1.left");var subQ10=sQuery(id+"F0.wireOp",EDGE,"E23.filletArc");var subQ11=sQuery(id+"F0.wireOp",EDGE,"E24.filletArc");Q0=makeQuery(id+"F2.boolean.opBoolean","SPLIT",FACE,{"disambiguationData":[TD([makeQuery(id+"F1.opExtrude","SWEPT_FACE",FACE,{"disambiguationData":[OSD([subQ6])]})])],"derivedFrom":makeQuery(id+"F1.opExtrude","CAP_FACE",FACE,{"disambiguationData":[OSD([subQ6,subQ8,subQ9,subQ7,subQ4,subQ3,subQ2,subQ1,subQ0,subQ5,subQ10,subQ11])],"isStart":true})});}
            var sketch = newSketch(context, id + "F16", { "sketchPlane" : qUnion([Q0])});
            skLineSegment(sketch, "E79", {"start": v(0, 90) * mm, "end": v(0, 98.12) * mm, "construction": true});
            skLineSegment(sketch, "E80", {"start": v(-15, 108) * mm, "end": v(-33, 90) * mm});
            skLineSegment(sketch, "E81", {"start": v(15, 108) * mm, "end": v(33, 90) * mm});
            skLineSegment(sketch, "E82", {"start": v(-15, 119.81) * mm, "end": v(-15, 108) * mm});
            skLineSegment(sketch, "E83", {"start": v(15, 119.81) * mm, "end": v(15, 108) * mm});
            skCircle(sketch, "E84", {"center": v(0, 120) * mm, "radius": 6 * mm});
            skArc(sketch, "E85", {"start": v(15, 119.81) * mm, "mid": v(0, 134.81) * mm, "end": v(-15, 119.81) * mm});
            skLineSegment(sketch, "E86", {"start": v(-80, 0) * mm, "end": v(80, 0) * mm, "construction": true});
            skLineSegment(sketch, "E87.MirrorCS", {"start": v(15, -119.81) * mm, "end": v(15, -108) * mm});
            skLineSegment(sketch, "E88.MirrorCS", {"start": v(-15, -119.81) * mm, "end": v(-15, -108) * mm});
            skArc(sketch, "E89.MirrorCS", {"start": v(15, -119.81) * mm, "mid": v(0, -134.81) * mm, "end": v(-15, -119.81) * mm});
            skCircle(sketch, "E90.MirrorC", {"center": v(0, -120) * mm, "radius": 6 * mm});
            skLineSegment(sketch, "E91.MirrorCS", {"start": v(-15, -108) * mm, "end": v(-33, -90) * mm});
            skLineSegment(sketch, "E92.MirrorCS", {"start": v(15, -108) * mm, "end": v(33, -90) * mm});
            skLineSegment(sketch, "E93.MirrorCS", {"start": v(0, -90) * mm, "end": v(0, -98.12) * mm, "construction": true});
            skSolve(sketch);
        }
        {
            var Q0;
            {var subQ0=sQuery(id+"F16.wireOp",EDGE,"E80");Q0=makeQuery(id+"F16.imprint","IMPRINT",FACE,{"disambiguationData":[TD([[makeQuery(id+"F16.imprint","IMPRINT",EDGE,{"derivedFrom":subQ0}),1.0]])]});}
            var Q1;
            Q1=makeQuery(id+"F16.imprint","IMPRINT",FACE,{"disambiguationData":[TD([[makeQuery(id+"F16.imprint","IMPRINT",EDGE,{"derivedFrom":makeQuery(id+"F1.opExtrude","CAP_EDGE",EDGE,{"disambiguationData":[OSD([sQuery(id+"F0.wireOp",EDGE,"E1.left")])],"isStart":true})}),-1.0]])]});
            var Q2;
            Q2=makeQuery(id+"F16.imprint","IMPRINT",FACE,{"disambiguationData":[TD([[makeQuery(id+"F16.imprint","IMPRINT",EDGE,{"derivedFrom":sQuery(id+"F16.wireOp",EDGE,"E89.MirrorCS")}),-1.0]])]});
            var Q3;
            Q3=makeQuery(id+"F2.opExtrude","CAP_FACE",FACE,{"disambiguationData":[OSD([sQuery(id+"F0.wireOp",EDGE,"E12"),sQuery(id+"F0.wireOp",EDGE,"E13"),sQuery(id+"F0.wireOp",EDGE,"E14"),sQuery(id+"F0.wireOp",EDGE,"E15"),sQuery(id+"F0.wireOp",EDGE,"E17.filletArc"),sQuery(id+"F0.wireOp",EDGE,"E18.filletArc"),sQuery(id+"F0.wireOp",EDGE,"E19.filletArc"),sQuery(id+"F0.wireOp",EDGE,"E20.filletArc"),sQuery(id+"F0.wireOp",EDGE,"E25.0"),sQuery(id+"F0.wireOp",EDGE,"E25.1"),sQuery(id+"F0.wireOp",EDGE,"E25.2"),sQuery(id+"F0.wireOp",EDGE,"E25.3"),sQuery(id+"F0.wireOp",EDGE,"E25.4"),sQuery(id+"F0.wireOp",EDGE,"E25.5"),sQuery(id+"F0.wireOp",EDGE,"E25.6"),sQuery(id+"F0.wireOp",EDGE,"E25.7")])],"isStart":false});
            extrude(context, id + "F17", {"entities" : qUnion([Q0, Q1, Q2]), "endBound" : BoundingType.UP_TO_SURFACE, "depth" : 25 * mm, "endBoundEntityFace" : qUnion([Q3]), "offsetDistance" : 25 * mm});
        }
    });
